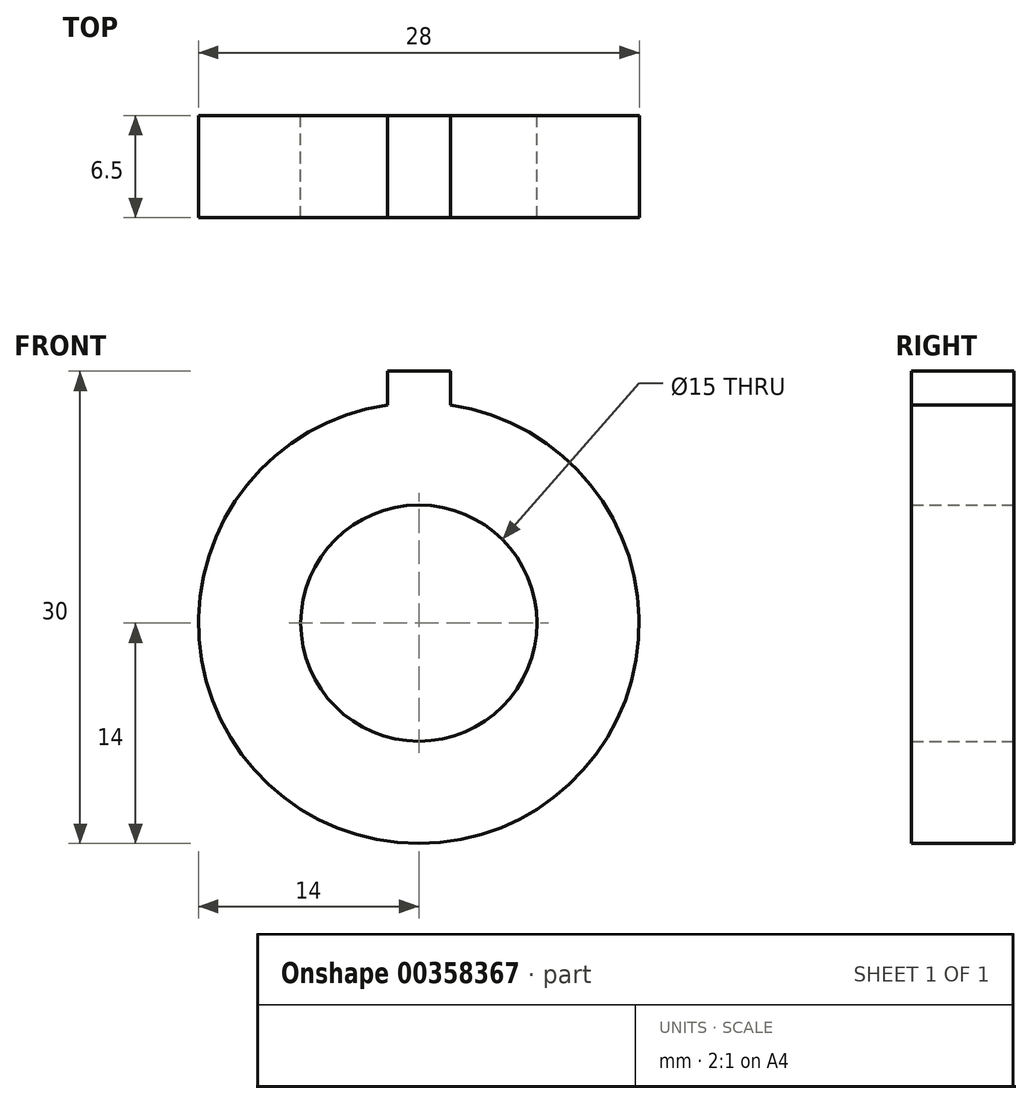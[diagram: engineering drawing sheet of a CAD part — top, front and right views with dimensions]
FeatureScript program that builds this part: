
annotation { "Feature Type Name" : "Feature", "Feature Type Description" : "" }
export const myFeature = defineFeature(function(context is Context, id is Id, definition is map)
    precondition{}
    {
        {
            var Q0;
            Q0=qCreatedBy(makeId("Front.planeOp"),FACE);
            var sketch = newSketch(context, id + "F0", { "sketchPlane" : qUnion([Q0])});
            skArc(sketch, "E0", {"start": v(-2, 13.86) * mm, "mid": v(0, -14) * mm, "end": v(2, 13.86) * mm});
            skCircle(sketch, "E1", {"center": v(0, 0) * mm, "radius": 7.5 * mm});
            skLineSegment(sketch, "E2", {"start": v(-2, 16) * mm, "end": v(2, 16) * mm});
            skLineSegment(sketch, "E3.trimOffspring", {"start": v(-2, 13.86) * mm, "end": v(-2, 16) * mm});
            skLineSegment(sketch, "E4.trimOffspring", {"start": v(2, 13.86) * mm, "end": v(2, 16) * mm});
            skSolve(sketch);
        }
        {
            var Q0;
            Q0=makeQuery(id+"F0.imprint","IMPRINT",FACE,{"disambiguationData":[TD([[makeQuery(id+"F0.imprint","IMPRINT",EDGE,{"derivedFrom":sQuery(id+"F0.wireOp",EDGE,"E0")}),1.0]])]});
            extrude(context, id + "F1", {"entities" : qUnion([Q0]), "depth" : 3.25 * mm, "hasSecondDirection" : true, "secondDirectionOppositeDirection" : true, "secondDirectionDepth" : 3.25 * mm});
        }
    });
